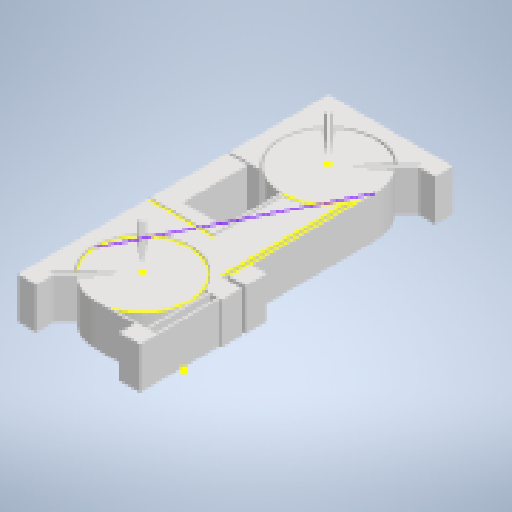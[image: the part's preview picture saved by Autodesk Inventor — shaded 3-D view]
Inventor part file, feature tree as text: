
AUTODESK INVENTOR PART (.ipt)
format: ipt  version: 2023 (Build 270158000, 158)  size: 383,488 bytes
history: native  units: mm
features: extrude x4, sketch x3, other x3, reference x2
ambient origin geometry x8: Origin, YZ Plane, XZ Plane, XY Plane, X Axis, Y Axis, Z Axis, Center Point
bodies: Solid1 (feature_tree)
feature tree (12):
  extrude  "Extrusion1"  Depth=150.0mm
  extrude  "Extrusion2"  Depth=20.0mm
  extrude  "Extrusion3"  Depth=150.0mm
  extrude  "Extrusion4"  Depth=10.0mm TaperAngle=0.0deg
  sketch  "Sketch1"  dims[d0=100.0mm d1=150.0mm]
  sketch  "Sketch6"  dims[d2=20.0mm d3=20.0mm]
  sketch  "Sketch7"  dims[d4=150.0mm d5=150.0mm d6=10.0mm d7=0.0mm d18=45.0mm d19=45.0mm d21=47.0mm d22=47.0mm d23=1.0mm d24=1.0mm d25=10.0mm d26=30.0mm d27=1.0mm d28=1.0mm d29=1.0mm d31=50.0mm d32=7.5mm d34=2.0mm d35=2.0mm d36=0.5mm d37=0.5mm d39=3.0mm d40=3.0mm d41=45.0deg d43=30.0mm d44=45.0deg d45=10.0mm d46=1.0mm d47=1.0mm d48=1.0mm d49=0.5mm d50=0.5mm d51=1.0mm d52=1.0mm d53=8.5mm d58=0.5mm d59=0.5mm d60=1.0mm d61=1.0mm d62=0.5mm d63=0.5mm d64=1.0mm d65=1.0mm d66=8.5mm d67=8.5mm d68=30.0mm d69=30.0mm d70=30.0mm d71=8.5mm d72=8.5mm d73=0.5mm d74=0.5mm d75=1.0mm d76=1.0mm d77=0.872665mm d78=0.872665mm d79=0.872665mm d80=0.872665mm d81=0.872665mm d82=0.872665mm d83=0.872665mm d84=0.872665mm d85=20.0mm d86=0.0mm d94=4.0mm d95=4.0mm d96=2.65mm d97=4.0mm d98=4.0mm d99=2.65mm d100=0.0mm d101=2.65mm d102=40.0mm d103=2.65mm d104=2.65mm d105=2.65mm d106=4.0mm d107=4.0mm d108=4.0mm d109=4.0mm d110=4.0mm d111=4.0mm d112=10.0mm d113=0.0mm d114=2.65mm d115=2.65mm d116=10.0mm d117=0.0mm]
  reference  "Reference1"
  reference  "Reference2"
  other  "<userpath>\ClawdDrive\Objet3D\IminaProbe\V2\FlexK7V2.iam"
  other  "FlexK7V2.iam"
  other  "FlexK7Holder:1"
